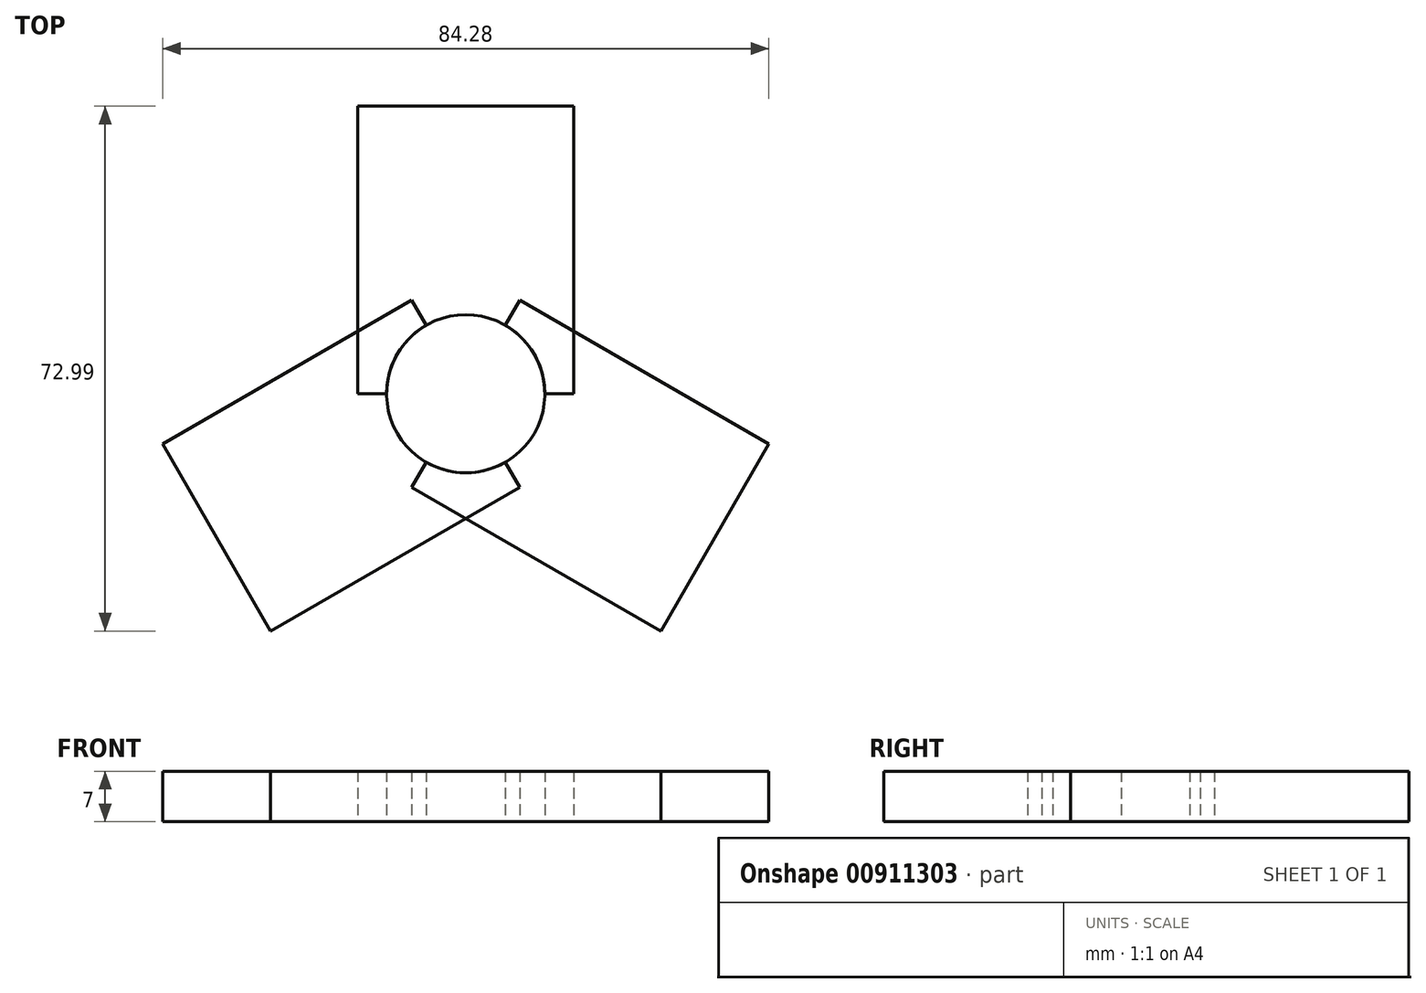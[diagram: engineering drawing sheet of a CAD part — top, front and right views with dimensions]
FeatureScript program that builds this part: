
annotation { "Feature Type Name" : "Feature", "Feature Type Description" : "" }
export const myFeature = defineFeature(function(context is Context, id is Id, definition is map)
    precondition{}
    {
        {
            var Q0;
            Q0=qCreatedBy(makeId("Top.planeOp"),FACE);
            var sketch = newSketch(context, id + "F0", { "sketchPlane" : qUnion([Q0])});
            skCircle(sketch, "E0", {"center": v(0, 0) * mm, "radius": 11 * mm});
            skLineSegment(sketch, "E1", {"start": v(0, 0) * mm, "end": v(0, 40) * mm});
            skLineSegment(sketch, "E2", {"start": v(0, 40) * mm, "end": v(15, 40) * mm});
            skLineSegment(sketch, "E3", {"start": v(15, 40) * mm, "end": v(15, 0) * mm});
            skLineSegment(sketch, "E4", {"start": v(15, 0) * mm, "end": v(0, 0) * mm});
            skLineSegment(sketch, "E5", {"start": v(0, 0) * mm, "end": v(-15, 0) * mm});
            skLineSegment(sketch, "E6", {"start": v(-15, 0) * mm, "end": v(-15, 40) * mm});
            skLineSegment(sketch, "E7", {"start": v(-15, 40) * mm, "end": v(0, 40) * mm});
            skSolve(sketch);
        }
        {
            var Q0;
            {var subQ0=sQuery(id+"F0.wireOp",EDGE,"E6");Q0=makeQuery(id+"F0.imprint","IMPRINT",FACE,{"disambiguationData":[TD([[makeQuery(id+"F0.imprint","IMPRINT",EDGE,{"derivedFrom":subQ0}),-1.0]])]});}
            var Q1;
            {var subQ1=sQuery(id+"F0.wireOp",EDGE,"E2");Q1=makeQuery(id+"F0.imprint","IMPRINT",FACE,{"disambiguationData":[TD([[makeQuery(id+"F0.imprint","IMPRINT",EDGE,{"derivedFrom":subQ1}),-1.0]])]});}
            extrude(context, id + "F1", {"entities" : qUnion([Q0, Q1]), "depth" : 7 * mm, "offsetDistance" : 25 * mm});
        }
        {
            var Q0;
            Q0=qCreatedBy(makeId("Front.planeOp"),FACE);
            var sketch = newSketch(context, id + "F2", { "sketchPlane" : qUnion([Q0])});
            skLineSegment(sketch, "E8", {"start": v(0, 0) * mm, "end": v(0, 51.99) * mm});
            skSolve(sketch);
        }
        {
            var Q0;
            Q0=makeQuery(id+"F1.opExtrude","SWEPT_BODY",BODY,{"disambiguationData":[OSD([sQuery(id+"F0.wireOp",EDGE,"E0"),sQuery(id+"F0.wireOp",EDGE,"E2"),sQuery(id+"F0.wireOp",EDGE,"E3"),sQuery(id+"F0.wireOp",EDGE,"E4"),sQuery(id+"F0.wireOp",EDGE,"E5"),sQuery(id+"F0.wireOp",EDGE,"E6"),sQuery(id+"F0.wireOp",EDGE,"E7")])]});
            var Q1;
            Q1=sQuery(id+"F2.wireOp",EDGE,"E8");
            transform(context, id + "F3", {"entities" : qUnion([Q0]), "transformType" : TransformType.ROTATION, "transformAxis" : qUnion([Q1]), "angle" : 120 * degree, "makeCopy" : true});
        }
        {
            var Q0;
            Q0=qCreatedBy(makeId("Front.planeOp"),FACE);
            var sketch = newSketch(context, id + "F4", { "sketchPlane" : qUnion([Q0])});
            skLineSegment(sketch, "E9", {"start": v(0, 0) * mm, "end": v(0, 31.84) * mm});
            skSolve(sketch);
        }
        {
            var Q0;
            Q0=makeQuery(id+"F1.opExtrude","SWEPT_BODY",BODY,{"disambiguationData":[OSD([sQuery(id+"F0.wireOp",EDGE,"E0"),sQuery(id+"F0.wireOp",EDGE,"E2"),sQuery(id+"F0.wireOp",EDGE,"E3"),sQuery(id+"F0.wireOp",EDGE,"E4"),sQuery(id+"F0.wireOp",EDGE,"E5"),sQuery(id+"F0.wireOp",EDGE,"E6"),sQuery(id+"F0.wireOp",EDGE,"E7")])]});
            var Q1;
            Q1=sQuery(id+"F4.wireOp",EDGE,"E9");
            transform(context, id + "F5", {"entities" : qUnion([Q0]), "transformType" : TransformType.ROTATION, "transformAxis" : qUnion([Q1]), "angle" : 240 * degree, "makeCopy" : true});
        }
    });
